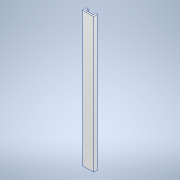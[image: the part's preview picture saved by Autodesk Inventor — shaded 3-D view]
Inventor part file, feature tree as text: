
AUTODESK INVENTOR PART (.ipt)
format: ipt  version: 2022 (Build 260153000, 153)  size: 103,936 bytes
history: native  units: mm
features: extrude x1, sketch x1
ambient origin geometry x8: Origin, YZ Plane, XZ Plane, XY Plane, X Axis, Y Axis, Z Axis, Center Point
bodies: Solid1 (feature_tree)
feature tree (2):
  extrude  "Extrusion1"  Depth=80.0mm
  sketch  "Sketch1"  dims[d0=15.0mm d1=80.0mm d2=950.0mm d3=0.0mm]
